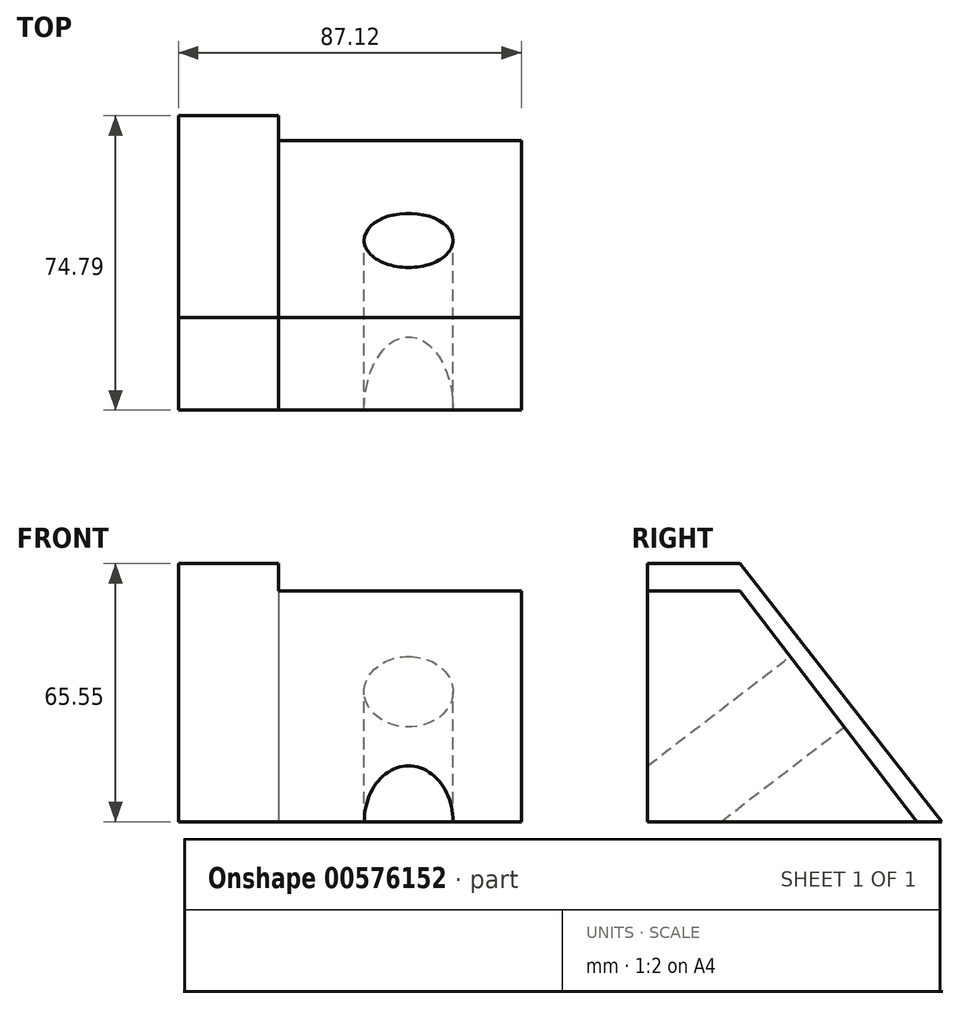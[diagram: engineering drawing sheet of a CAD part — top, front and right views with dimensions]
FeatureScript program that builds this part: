
annotation { "Feature Type Name" : "Feature", "Feature Type Description" : "" }
export const myFeature = defineFeature(function(context is Context, id is Id, definition is map)
    precondition{}
    {
        {
            var Q0;
            Q0=qCreatedBy(makeId("Right.planeOp"),FACE);
            var sketch = newSketch(context, id + "F0", { "sketchPlane" : qUnion([Q0])});
            skLineSegment(sketch, "E0.bottom", {"start": v(0, 0) * mm, "end": v(-23.5, 0) * mm});
            skLineSegment(sketch, "E0.top", {"start": v(0, 65.55) * mm, "end": v(-23.5, 65.55) * mm});
            skLineSegment(sketch, "E0.left", {"start": v(0, 0) * mm, "end": v(0, 65.55) * mm});
            skLineSegment(sketch, "E0.right", {"start": v(-23.5, 0) * mm, "end": v(-23.5, 65.55) * mm});
            skLineSegment(sketch, "E1", {"start": v(0, 65.55) * mm, "end": v(51.29, 0) * mm});
            skLineSegment(sketch, "E2", {"start": v(51.29, 0) * mm, "end": v(0, 0) * mm});
            skSolve(sketch);
        }
        {
            var Q0;
            Q0=makeQuery(id+"F0.imprint","IMPRINT",FACE,{"disambiguationData":[TD([[makeQuery(id+"F0.imprint","IMPRINT",EDGE,{"derivedFrom":sQuery(id+"F0.wireOp",EDGE,"E0.left")}),-1.0]])]});
            var Q1;
            Q1=makeQuery(id+"F0.imprint","IMPRINT",FACE,{"disambiguationData":[TD([[makeQuery(id+"F0.imprint","IMPRINT",EDGE,{"derivedFrom":sQuery(id+"F0.wireOp",EDGE,"E0.bottom")}),-1.0]])]});
            extrude(context, id + "F1", {"entities" : qUnion([Q0, Q1]), "depth" : 25.4 * mm, "offsetDistance" : 25.4 * mm});
        }
        {
            var Q0;
            Q0=makeQuery(id+"F1.opExtrude","CAP_FACE",FACE,{"disambiguationData":[OSD([sQuery(id+"F0.wireOp",EDGE,"E0.bottom"),sQuery(id+"F0.wireOp",EDGE,"E0.top"),sQuery(id+"F0.wireOp",EDGE,"E0.right"),sQuery(id+"F0.wireOp",EDGE,"E1"),sQuery(id+"F0.wireOp",EDGE,"E2")])],"isStart":false});
            var sketch = newSketch(context, id + "F2", { "sketchPlane" : qUnion([Q0])});
            skLineSegment(sketch, "E3", {"start": v(-23.5, 58.65) * mm, "end": v(0, 58.65) * mm});
            skLineSegment(sketch, "E4", {"start": v(0, 58.65) * mm, "end": v(44.95, 0) * mm});
            skLineSegment(sketch, "E5", {"start": v(44.95, 0) * mm, "end": v(-23.5, 0) * mm});
            skLineSegment(sketch, "E6", {"start": v(-23.5, 0) * mm, "end": v(-23.5, 58.65) * mm});
            skSolve(sketch);
        }
        {
            var Q0;
            Q0=makeQuery(id+"F2.imprint","IMPRINT",FACE,{"disambiguationData":[TD([[makeQuery(id+"F2.imprint","IMPRINT",EDGE,{"derivedFrom":sQuery(id+"F2.wireOp",EDGE,"E3")}),-1.0]])]});
            extrude(context, id + "F3", {"entities" : qUnion([Q0]), "operationType" : NewBodyOperationType.ADD, "depth" : 61.72 * mm, "offsetDistance" : 25.4 * mm});
        }
        {
            var Q0;
            Q0=makeQuery(id+"F3.opExtrude","SWEPT_FACE",FACE,{"disambiguationData":[OSD([sQuery(id+"F2.wireOp",EDGE,"E4")])]});
            var sketch = newSketch(context, id + "F4", { "sketchPlane" : qUnion([Q0])});
            skCircle(sketch, "E7", {"center": v(-58.48, 14.24) * mm, "radius": 11.3 * mm});
            skSolve(sketch);
        }
        {
            var Q0;
            Q0 = qSketchRegion(id + "F4", true);
            extrude(context, id + "F5", {"entities" : qUnion([Q0]), "operationType" : NewBodyOperationType.REMOVE, "oppositeDirection" : true, "depth" : 63.75 * mm, "offsetDistance" : 25.4 * mm});
        }
    });
